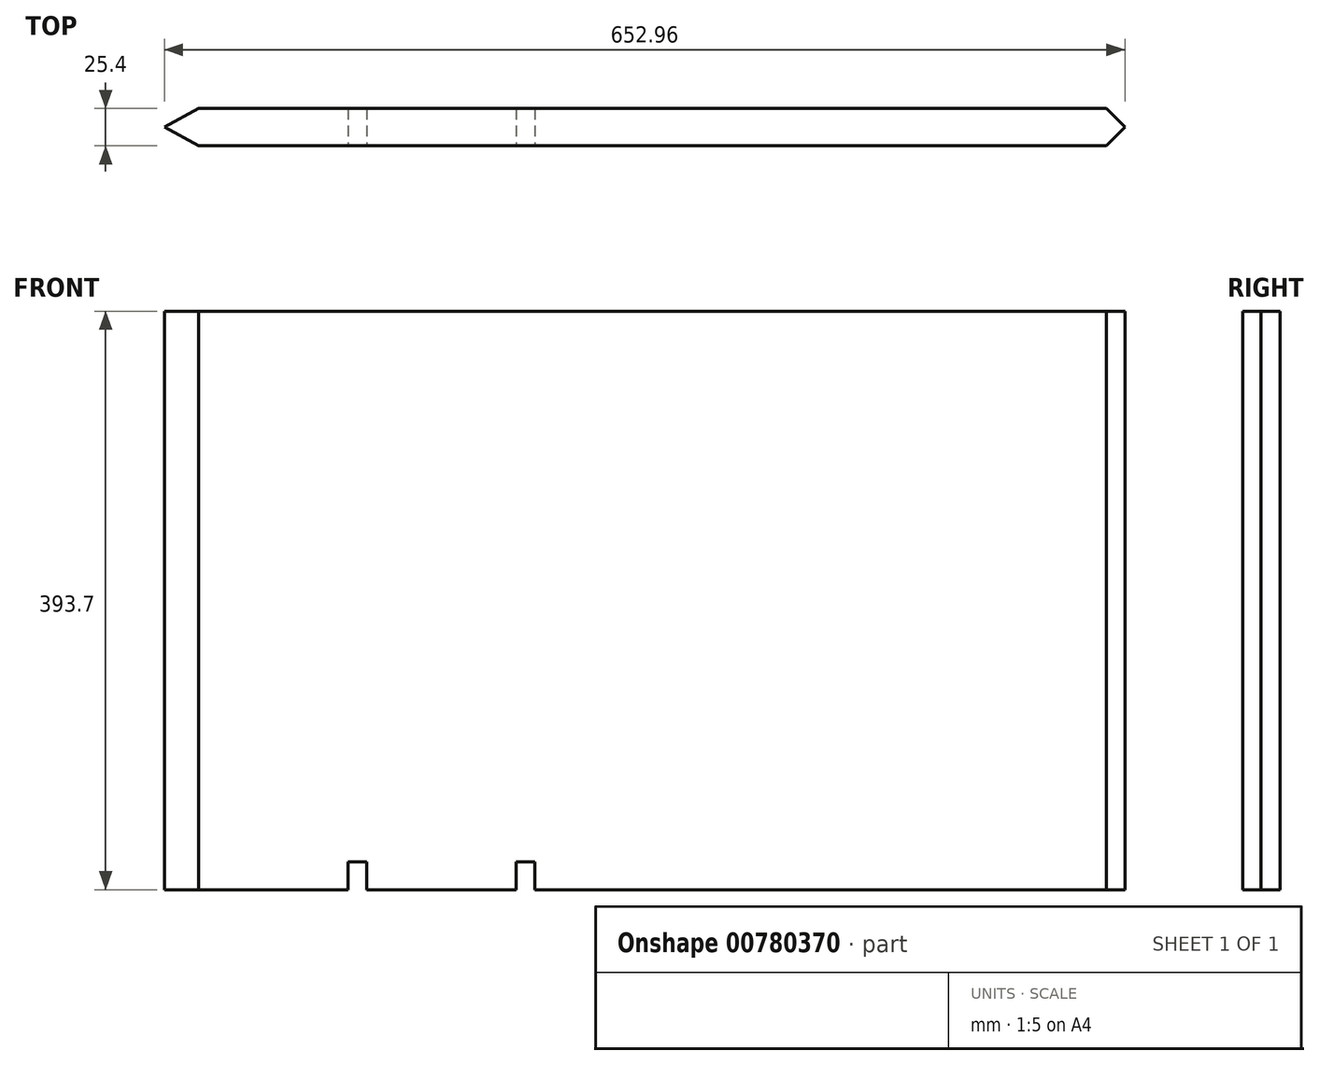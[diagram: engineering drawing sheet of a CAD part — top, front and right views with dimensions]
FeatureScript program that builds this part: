
annotation { "Feature Type Name" : "Feature", "Feature Type Description" : "" }
export const myFeature = defineFeature(function(context is Context, id is Id, definition is map)
    precondition{}
    {
        {
            var Q0;
            Q0=qCreatedBy(makeId("Top.planeOp"),FACE);
            var sketch = newSketch(context, id + "F0", { "sketchPlane" : qUnion([Q0])});
            skLineSegment(sketch, "E0.0", {"start": v(9.7, -12.7) * mm, "end": v(550.53, -12.7) * mm});
            skLineSegment(sketch, "E1.0", {"start": v(9.7, 12.7) * mm, "end": v(550.53, 12.7) * mm});
            skLineSegment(sketch, "E2", {"start": v(-13.53, 0) * mm, "end": v(9.7, 12.7) * mm});
            skLineSegment(sketch, "E3", {"start": v(-13.53, 0) * mm, "end": v(9.7, -12.7) * mm});
            skLineSegment(sketch, "E4", {"start": v(111.3, 12.7) * mm, "end": v(111.3, -12.7) * mm});
            skLineSegment(sketch, "E5.0", {"start": v(124, 12.7) * mm, "end": v(124, -12.7) * mm});
            skLineSegment(sketch, "E6", {"start": v(225.6, 12.7) * mm, "end": v(225.6, -12.7) * mm});
            skLineSegment(sketch, "E7.0", {"start": v(238.3, 12.7) * mm, "end": v(238.3, -12.7) * mm});
            skLineSegment(sketch, "E8", {"start": v(626.73, 12.7) * mm, "end": v(639.43, 0) * mm});
            skLineSegment(sketch, "E9", {"start": v(626.73, -12.7) * mm, "end": v(639.43, 0) * mm});
            skLineSegment(sketch, "E10", {"start": v(550.53, 12.7) * mm, "end": v(626.73, 12.7) * mm});
            skLineSegment(sketch, "E11", {"start": v(550.53, -12.7) * mm, "end": v(626.73, -12.7) * mm});
            skSolve(sketch);
        }
        {
            var Q0;
            {var subQ0=sQuery(id+"F0.wireOp",EDGE,"E7.0");Q0=makeQuery(id+"F0.imprint","IMPRINT",FACE,{"disambiguationData":[TD([[makeQuery(id+"F0.imprint","IMPRINT",EDGE,{"derivedFrom":subQ0}),1.0]])]});}
            var Q1;
            {var subQ0=sQuery(id+"F0.wireOp",EDGE,"E6");Q1=makeQuery(id+"F0.imprint","IMPRINT",FACE,{"disambiguationData":[TD([[makeQuery(id+"F0.imprint","IMPRINT",EDGE,{"derivedFrom":subQ0}),1.0]])]});}
            var Q2;
            {var subQ0=sQuery(id+"F0.wireOp",EDGE,"E5.0");Q2=makeQuery(id+"F0.imprint","IMPRINT",FACE,{"disambiguationData":[TD([[makeQuery(id+"F0.imprint","IMPRINT",EDGE,{"derivedFrom":subQ0}),1.0]])]});}
            var Q3;
            {var subQ0=sQuery(id+"F0.wireOp",EDGE,"E4");Q3=makeQuery(id+"F0.imprint","IMPRINT",FACE,{"disambiguationData":[TD([[makeQuery(id+"F0.imprint","IMPRINT",EDGE,{"derivedFrom":subQ0}),1.0]])]});}
            var Q4;
            {var subQ3=sQuery(id+"F0.wireOp",EDGE,"E2");Q4=makeQuery(id+"F0.imprint","IMPRINT",FACE,{"disambiguationData":[TD([[makeQuery(id+"F0.imprint","IMPRINT",EDGE,{"derivedFrom":subQ3}),-1.0]])]});}
            extrude(context, id + "F1", {"entities" : qUnion([Q0, Q1, Q2, Q3, Q4]), "depth" : 374.65 * mm, "offsetDistance" : 25.4 * mm});
        }
        {
            var Q0;
            {var subQ0=sQuery(id+"F0.wireOp",EDGE,"E7.0");Q0=makeQuery(id+"F0.imprint","IMPRINT",FACE,{"disambiguationData":[TD([[makeQuery(id+"F0.imprint","IMPRINT",EDGE,{"derivedFrom":subQ0}),1.0]])]});}
            var Q1;
            {var subQ0=sQuery(id+"F0.wireOp",EDGE,"E5.0");Q1=makeQuery(id+"F0.imprint","IMPRINT",FACE,{"disambiguationData":[TD([[makeQuery(id+"F0.imprint","IMPRINT",EDGE,{"derivedFrom":subQ0}),1.0]])]});}
            var Q2;
            {var subQ3=sQuery(id+"F0.wireOp",EDGE,"E2");Q2=makeQuery(id+"F0.imprint","IMPRINT",FACE,{"disambiguationData":[TD([[makeQuery(id+"F0.imprint","IMPRINT",EDGE,{"derivedFrom":subQ3}),-1.0]])]});}
            extrude(context, id + "F2", {"entities" : qUnion([Q0, Q1, Q2]), "operationType" : NewBodyOperationType.ADD, "oppositeDirection" : true, "depth" : 19.05 * mm, "offsetDistance" : 25.4 * mm});
        }
    });
